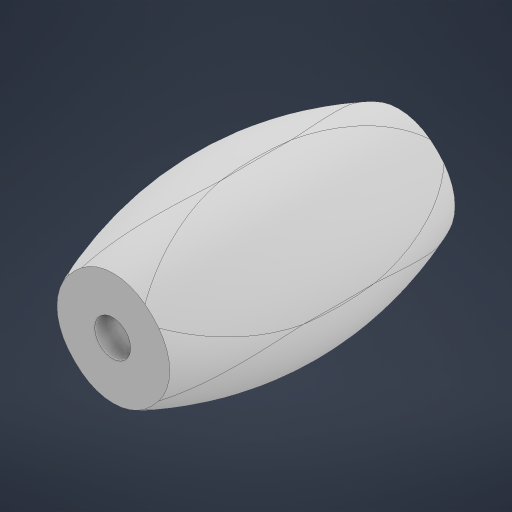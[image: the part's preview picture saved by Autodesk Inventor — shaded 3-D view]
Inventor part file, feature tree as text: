
AUTODESK INVENTOR PART (.ipt)
format: ipt  version: 2023 (Build 270158000, 158)  size: 445,952 bytes
history: native  units: mm
features: extrude x5, sketch x4, fillet x2
ambient origin geometry x8: Origin, YZ Plane, XZ Plane, XY Plane, X Axis, Y Axis, Z Axis, Center Point
bodies: Solid1 (feature_tree)
feature tree (11):
  extrude  "Extrusion1"  Depth=15.0mm
  sketch  "Sketch2"  dims[d2=25.4mm d3=0.0mm d4=2.0mm]
  extrude  "Extrusion2"  Depth=2.0mm
  extrude  "Extrusion3"  Depth=2.0mm
  extrude  "Extrusion4"  Depth=25.4mm TaperAngle=0.0deg
  fillet  "Fillet1"  Radius=25.4mm
  fillet  "Fillet2"  Radius=25.4mm
  extrude  "Extrusion5"  Depth=7.4mm
  sketch  "Sketch1"  dims[d0=15.0mm d1=15.0mm]
  sketch  "Sketch3"  dims[d5=2.0mm d6=2.0mm]
  sketch  "Sketch4"  dims[d7=2.0mm d8=25.4mm d9=0.0mm d10=25.4mm d11=0.0mm d12=25.4mm d13=0.0mm d14=7.4mm d15=5.0mm d16=3.2mm d17=25.4mm d18=0.0mm]
